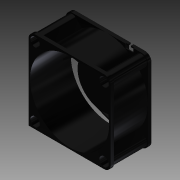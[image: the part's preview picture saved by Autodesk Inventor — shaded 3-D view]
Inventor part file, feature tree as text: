
AUTODESK INVENTOR PART (.ipt)
format: ipt  version: 2014 (Build 180170000, 170)  size: 280,576 bytes
history: native  units: mm (DEFAULTED — no unit token found)
features: sketch x10, extrude x9, plane x1, revolve x1, fillet x1, pattern_circular x1, other x1, projected_geometry x1
ambient origin geometry x8: Origin, YZ Plane, XZ Plane, XY Plane, X Axis, Y Axis, Z Axis, Center Point
bodies: Solid1 (feature_tree)
feature tree (25):
  extrude  "Extrusion1"  Depth=39.878mm
  plane  "Work Plane1"
  revolve  "Revolution1"  [1 undecoded]
  fillet  "Fillet1"  Radius=1.7018mm
  extrude  "Extrusion2"  TaperAngle=90.0deg  [1 undecoded]
  extrude  "Extrusion3"  Depth=3.175mm
  pattern_circular  "Circular Pattern1"  Count=4 Angle=360.0deg
  extrude  "Extrusion4"  Depth=19.812mm
  extrude  "fan support1"  Depth=0.635mm
  extrude  "fan support2"  Depth=3.81mm TaperAngle=0.0deg
  extrude  "fan support3"  Depth=8.001mm
  extrude  "fan support4"  Depth=1.5875mm
  extrude  "fan support5"  Depth=1.5875mm TaperAngle=0.0deg
  other  "fan interface"
  sketch  "Sketch1"  dims[d0=39.878mm d1=39.878mm]
  sketch  "Sketch2"  dims[d2=19.812mm d3=0.0mm d4=1.7018mm d5=1.7018mm]
  sketch  "Sketch3"  dims[d6=12.7mm d7=90.0deg]
  sketch  "Sketch4"  dims[d8=3.175mm d9=4.572mm]
  sketch  "Sketch5"  dims[d10=19.812mm d11=0.0mm]
  projected_geometry  "Projected Loop1"
  sketch  "Sketch6"  dims[d12=19.812mm d13=0.0mm d14=40.0mm d16=360.0deg]
  sketch  "Sketch7"  dims[d17=19.812mm d18=0.0mm d19=38.481mm]
  sketch  "Sketch8"  dims[d20=24.2824mm d21=0.635mm]
  sketch  "Sketch9"  dims[d23=0.635mm d24=3.81mm d25=0.0mm]
  sketch  "Sketch10"  dims[d26=5.08mm d27=8.001mm d28=4.0005mm d29=1.5875mm d30=0.0mm d31=22.896572mm d32=0.635mm d33=0.635mm d34=0.635mm d35=0.635mm d36=1.27mm d37=0.0mm d38=1.55575mm d39=0.0mm d40=1.55575mm d41=0.0mm d42=1.5875mm]
note: 2 required parameter values undecoded (feature->parameter linkage not recoverable at this tier; creation-order binding heuristic only, values carry confidence <= 0.55)